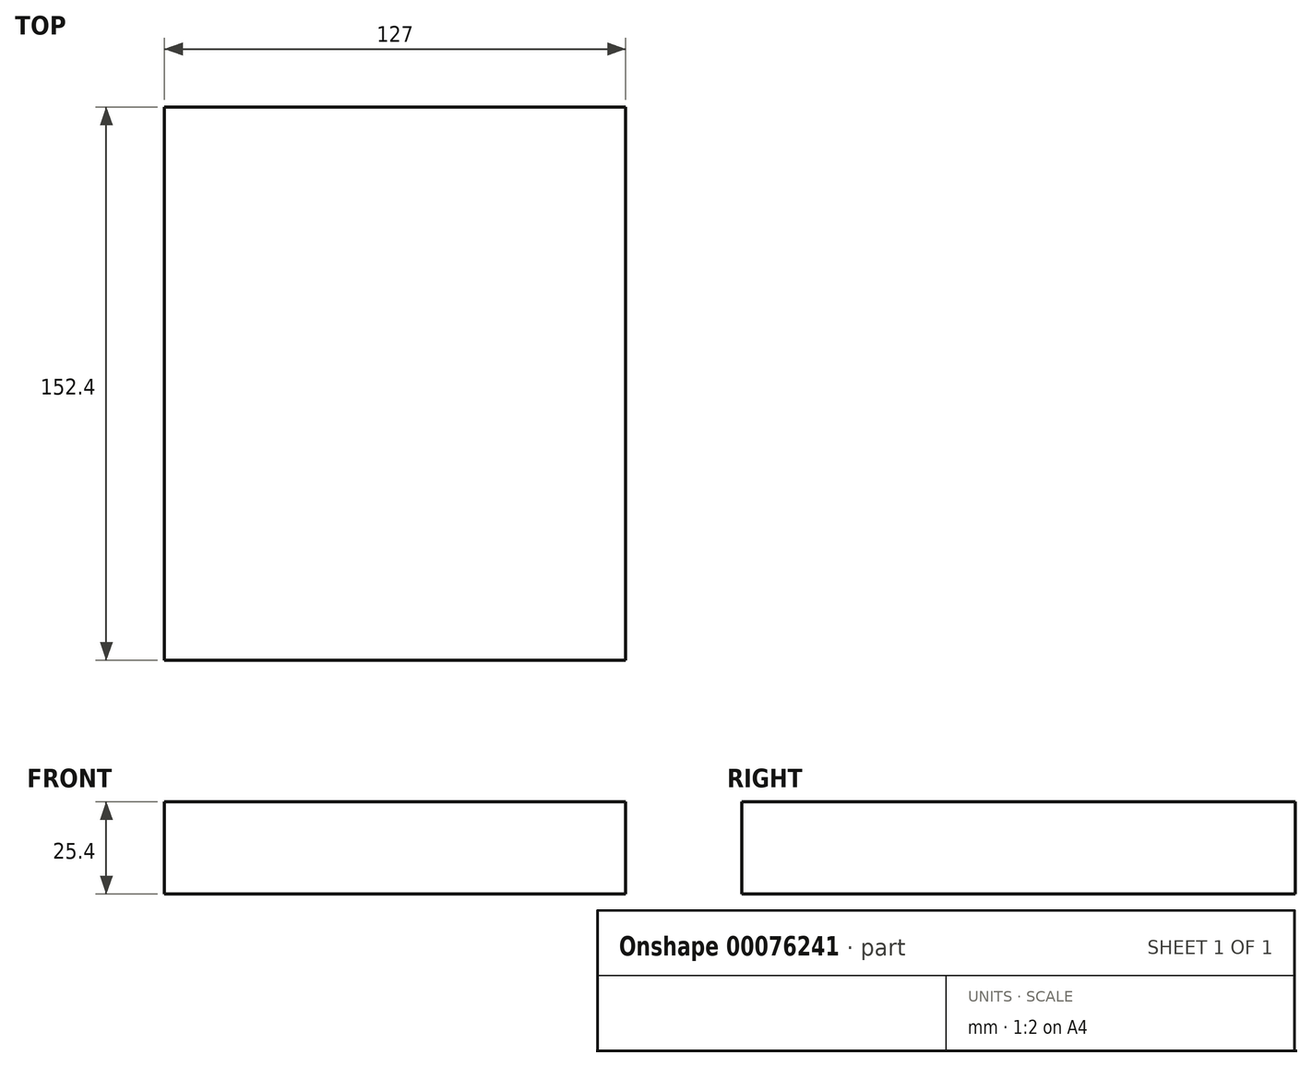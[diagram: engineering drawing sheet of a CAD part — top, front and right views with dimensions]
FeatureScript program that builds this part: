
annotation { "Feature Type Name" : "Feature", "Feature Type Description" : "" }
export const myFeature = defineFeature(function(context is Context, id is Id, definition is map)
    precondition{}
    {
        {
            var Q0;
            Q0=qCreatedBy(makeId("Front.planeOp"),FACE);
            var sketch = newSketch(context, id + "F0", { "sketchPlane" : qUnion([Q0])});
            skLineSegment(sketch, "E0.bottom", {"start": v(-61.72, 25.4) * mm, "end": v(65.28, 25.4) * mm});
            skLineSegment(sketch, "E0.top", {"start": v(-61.72, 0) * mm, "end": v(65.28, 0) * mm});
            skLineSegment(sketch, "E0.left", {"start": v(-61.72, 25.4) * mm, "end": v(-61.72, 0) * mm});
            skLineSegment(sketch, "E0.right", {"start": v(65.28, 25.4) * mm, "end": v(65.28, 0) * mm});
            skSolve(sketch);
        }
        {
            var Q0;
            Q0=makeQuery(id+"F0.imprint","IMPRINT",FACE,{"disambiguationData":[TD([[makeQuery(id+"F0.imprint","IMPRINT",EDGE,{"derivedFrom":sQuery(id+"F0.wireOp",EDGE,"E0.bottom")}),-1.0]])]});
            extrude(context, id + "F1", {"entities" : qUnion([Q0]), "depth" : 152.4 * mm});
        }
    });
